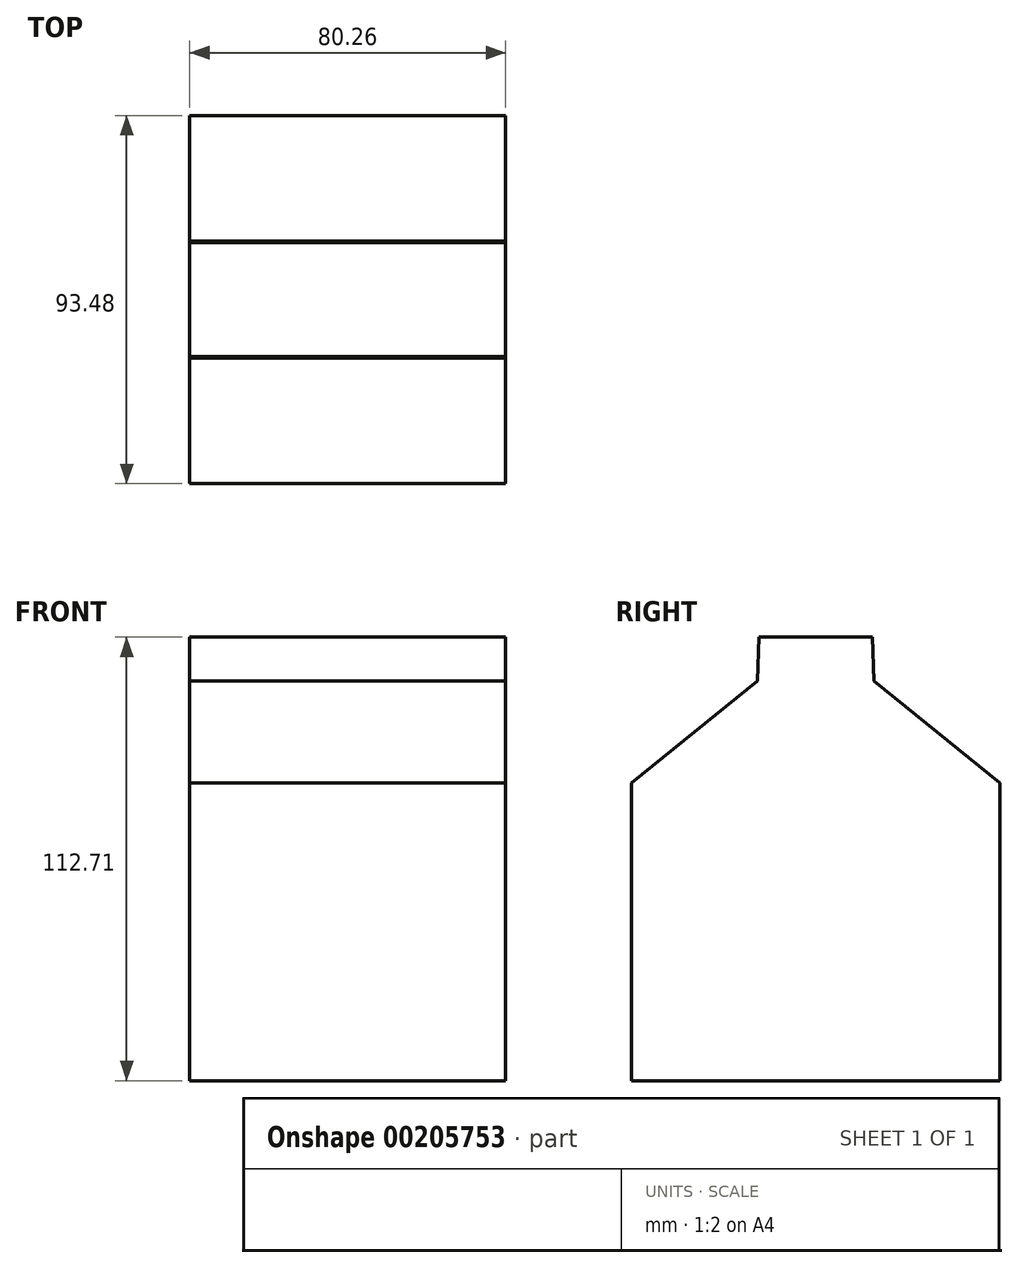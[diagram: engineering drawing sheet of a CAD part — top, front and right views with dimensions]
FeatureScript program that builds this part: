
annotation { "Feature Type Name" : "Feature", "Feature Type Description" : "" }
export const myFeature = defineFeature(function(context is Context, id is Id, definition is map)
    precondition{}
    {
        {
            var Q0;
            Q0=qCreatedBy(makeId("Right.planeOp"),FACE);
            var sketch = newSketch(context, id + "F0", { "sketchPlane" : qUnion([Q0])});
            skLineSegment(sketch, "E0.top", {"start": v(-46.74, -37.8) * mm, "end": v(46.74, -37.8) * mm});
            skLineSegment(sketch, "E0.left", {"start": v(-46.74, 37.8) * mm, "end": v(-46.74, -37.8) * mm});
            skLineSegment(sketch, "E0.right", {"start": v(46.74, 37.8) * mm, "end": v(46.74, -37.8) * mm});
            skPoint(sketch, "E0.middle", {"position": v(0, 0) * mm});
            skLineSegment(sketch, "E1", {"start": v(14.85, 63.8) * mm, "end": v(46.74, 37.8) * mm});
            skLineSegment(sketch, "E2", {"start": v(14.47, 74.92) * mm, "end": v(14.85, 63.8) * mm});
            skLineSegment(sketch, "E3.MirrorCS", {"start": v(-14.85, 63.8) * mm, "end": v(-46.74, 37.8) * mm});
            skLineSegment(sketch, "E4.MirrorCS", {"start": v(-14.47, 74.92) * mm, "end": v(-14.85, 63.8) * mm});
            skLineSegment(sketch, "E5", {"start": v(-14.47, 74.92) * mm, "end": v(14.47, 74.92) * mm});
            skSolve(sketch);
        }
        {
            var Q0;
            Q0=makeQuery(id+"F0.imprint","IMPRINT",FACE,{"disambiguationData":[TD([[makeQuery(id+"F0.imprint","IMPRINT",EDGE,{"derivedFrom":sQuery(id+"F0.wireOp",EDGE,"E0.top")}),1.0]])]});
            extrude(context, id + "F1", {"entities" : qUnion([Q0]), "endBound" : BoundingType.SYMMETRIC, "depth" : 80.26 * mm});
        }
    });
